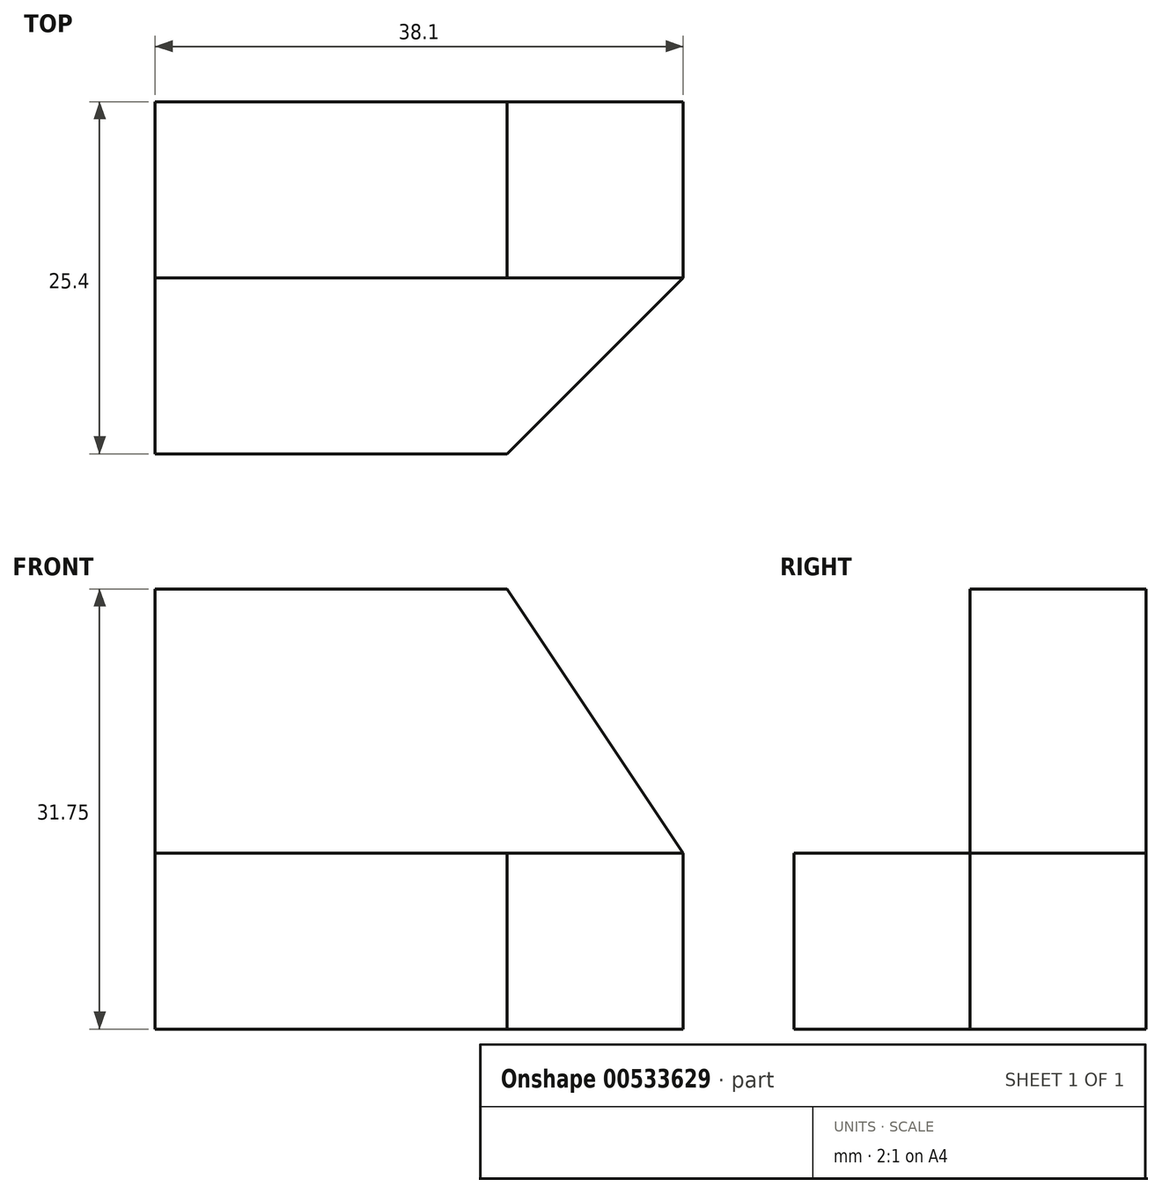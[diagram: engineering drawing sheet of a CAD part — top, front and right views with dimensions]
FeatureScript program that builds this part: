
annotation { "Feature Type Name" : "Feature", "Feature Type Description" : "" }
export const myFeature = defineFeature(function(context is Context, id is Id, definition is map)
    precondition{}
    {
        {
            var Q0;
            Q0=qCreatedBy(makeId("Front.planeOp"),FACE);
            var sketch = newSketch(context, id + "F0", { "sketchPlane" : qUnion([Q0])});
            skLineSegment(sketch, "E0", {"start": v(-52.98, 0) * mm, "end": v(-52.98, 31.75) * mm});
            skLineSegment(sketch, "E1", {"start": v(-52.98, 31.75) * mm, "end": v(-14.88, 31.75) * mm});
            skLineSegment(sketch, "E2", {"start": v(-14.88, 31.75) * mm, "end": v(-14.88, 0) * mm});
            skLineSegment(sketch, "E3", {"start": v(-14.88, 0) * mm, "end": v(-52.98, 0) * mm});
            skSolve(sketch);
        }
        {
            var Q0;
            Q0=makeQuery(id+"F0.imprint","IMPRINT",FACE,{"disambiguationData":[TD([[makeQuery(id+"F0.imprint","IMPRINT",EDGE,{"derivedFrom":sQuery(id+"F0.wireOp",EDGE,"E0")}),-1.0]])]});
            extrude(context, id + "F1", {"entities" : qUnion([Q0]), "depth" : 25.4 * mm, "offsetDistance" : 25.4 * mm});
        }
        {
            var Q0;
            Q0=makeQuery(id+"F1.opExtrude","CAP_FACE",FACE,{"disambiguationData":[OSD([sQuery(id+"F0.wireOp",EDGE,"E0"),sQuery(id+"F0.wireOp",EDGE,"E1"),sQuery(id+"F0.wireOp",EDGE,"E2"),sQuery(id+"F0.wireOp",EDGE,"E3")])],"isStart":false});
            var sketch = newSketch(context, id + "F2", { "sketchPlane" : qUnion([Q0])});
            skLineSegment(sketch, "E4", {"start": v(-52.98, 12.7) * mm, "end": v(-14.88, 12.7) * mm});
            skSolve(sketch);
        }
        {
            var Q0;
            {var subQ0=sQuery(id+"F2.wireOp",EDGE,"E4");Q0=makeQuery(id+"F2.imprint","IMPRINT",FACE,{"disambiguationData":[TD([[makeQuery(id+"F2.imprint","IMPRINT",EDGE,{"derivedFrom":subQ0}),1.0]])]});}
            extrude(context, id + "F3", {"entities" : qUnion([Q0]), "operationType" : NewBodyOperationType.REMOVE, "oppositeDirection" : true, "depth" : 12.7 * mm, "offsetDistance" : 25.4 * mm});
        }
        {
            var Q0;
            Q0=makeQuery(id+"F3.boolean.opBoolean","COPY",FACE,{"derivedFrom":makeQuery(id+"F3.opExtrude","CAP_FACE",FACE,{"disambiguationData":[OSD([sQuery(id+"F0.wireOp",EDGE,"E0"),sQuery(id+"F0.wireOp",EDGE,"E1"),sQuery(id+"F0.wireOp",EDGE,"E2"),sQuery(id+"F2.wireOp",EDGE,"E4")])],"isStart":false})});
            var sketch = newSketch(context, id + "F4", { "sketchPlane" : qUnion([Q0])});
            skLineSegment(sketch, "E5", {"start": v(-27.58, 31.75) * mm, "end": v(-14.88, 12.7) * mm});
            skSolve(sketch);
        }
        {
            var Q0;
            {var subQ0=sQuery(id+"F4.wireOp",EDGE,"E5");Q0=makeQuery(id+"F4.imprint","IMPRINT",FACE,{"disambiguationData":[TD([[makeQuery(id+"F4.imprint","IMPRINT",EDGE,{"derivedFrom":subQ0}),1.0]])]});}
            extrude(context, id + "F5", {"entities" : qUnion([Q0]), "operationType" : NewBodyOperationType.REMOVE, "endBound" : BoundingType.THROUGH_ALL, "oppositeDirection" : true, "depth" : 25.4 * mm, "offsetDistance" : 25.4 * mm});
        }
        {
            var Q0;
            Q0=makeQuery(id+"F3.boolean.opBoolean","COPY",FACE,{"derivedFrom":makeQuery(id+"F3.opExtrude","SWEPT_FACE",FACE,{"disambiguationData":[OSD([sQuery(id+"F2.wireOp",EDGE,"E4")])]})});
            var sketch = newSketch(context, id + "F6", { "sketchPlane" : qUnion([Q0])});
            skLineSegment(sketch, "E6", {"start": v(-14.88, -12.7) * mm, "end": v(-27.58, -25.4) * mm});
            skSolve(sketch);
        }
        {
            var Q0;
            {var subQ0=sQuery(id+"F6.wireOp",EDGE,"E6");Q0=makeQuery(id+"F6.imprint","IMPRINT",FACE,{"disambiguationData":[TD([[makeQuery(id+"F6.imprint","IMPRINT",EDGE,{"derivedFrom":subQ0}),1.0]])]});}
            extrude(context, id + "F7", {"entities" : qUnion([Q0]), "operationType" : NewBodyOperationType.REMOVE, "endBound" : BoundingType.THROUGH_ALL, "oppositeDirection" : true, "depth" : 25.4 * mm, "offsetDistance" : 25.4 * mm});
        }
    });
